FCSTD DOCUMENT  (FreeCAD 0.20R29410 (Git))
Label: slot
License: All rights reserved
LicenseURL: http://en.wikipedia.org/wiki/All_rights_reserved
objects: Part::Feature×1, Sketcher::SketchObject×1, PartDesign::Body×1
note: 3 computed .brp shape members not serialized (recipe doc carries the construction recipe); baked Part::Feature solids carry a one-line shape summary decoded from their .brp

FEATURE [Part::Feature] Feature  label="nascontrol-remote"
  shape: bbox 50.08 x 90 x 19.2 mm, 3250 faces, 43 solids (baked)
FEATURE [Sketcher::SketchObject] Sketch
  FullyConstrained = true
  MapMode = 5
  Placement = pos=(0,0,0) rot=(0.57735,0.57735,0.57735;2.0944rad)
  Support = -> [YZ_Plane]
  sketch-geometry (4):
    g0: LineSegment StartX=51.285 StartY=17.42 StartZ=0 EndX=-51.285 EndY=17.42 EndZ=0
    g1: LineSegment StartX=-51.285 StartY=17.42 StartZ=0 EndX=-51.285 EndY=-1 EndZ=0
    g2: LineSegment StartX=-51.285 StartY=-1 StartZ=0 EndX=51.285 EndY=-1 EndZ=0
    g3: LineSegment StartX=51.285 StartY=-1 StartZ=0 EndX=51.285 EndY=17.42 EndZ=0
  constraints (11):
    c: Coincident(g0,g1)
    c: Coincident(g1,g2)
    c: Coincident(g2,g3)
    c: Coincident(g3,g0)
    c: Horizontal(g2)
    c: Vertical(g1)
    c: Vertical(g3)
    c: DistanceX(g0,g0) = 102.57
    c: DistanceY(g3,g3) = 18.42
    c: Symmetric(g0,g0,g-2)
    c: DistanceY(g1,g-1) = 1
FEATURE [PartDesign::Body] Body
  Group = -> [Sketch]
  Origin = -> Origin
